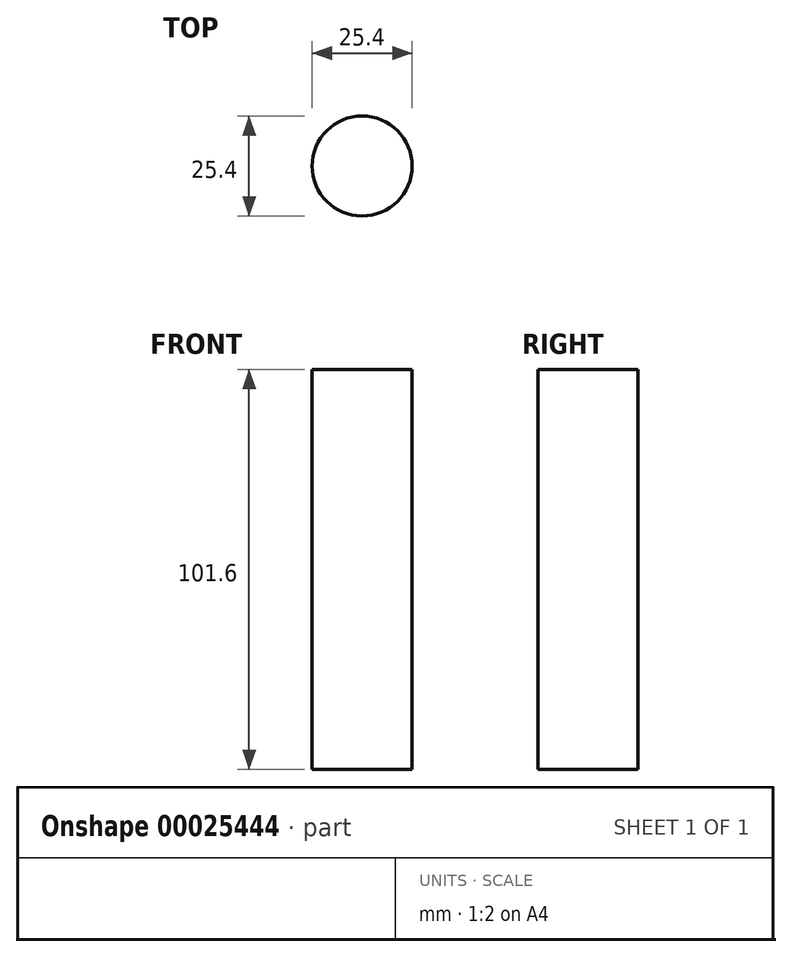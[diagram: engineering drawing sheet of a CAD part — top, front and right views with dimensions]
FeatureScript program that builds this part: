
annotation { "Feature Type Name" : "Feature", "Feature Type Description" : "" }
export const myFeature = defineFeature(function(context is Context, id is Id, definition is map)
    precondition{}
    {
        {
            var Q0;
            Q0=qCreatedBy(makeId("Top.planeOp"),FACE);
            var sketch = newSketch(context, id + "F0", { "sketchPlane" : qUnion([Q0])});
            skCircle(sketch, "E0", {"center": v(0, 0) * mm, "radius": 12.7 * mm});
            skSolve(sketch);
        }
        {
            var Q0;
            Q0=makeQuery(id+"F0.imprint","IMPRINT",FACE,{"disambiguationData":[TD([[makeQuery(id+"F0.imprint","IMPRINT",EDGE,{"derivedFrom":sQuery(id+"F0.wireOp",EDGE,"E0")}),1.0]])]});
            extrude(context, id + "F1", {"entities" : qUnion([Q0]), "depth" : 101.6 * mm});
        }
    });
